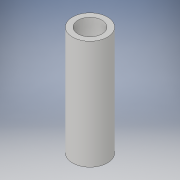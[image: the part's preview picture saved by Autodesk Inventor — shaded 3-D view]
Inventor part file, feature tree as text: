
AUTODESK INVENTOR PART (.ipt)
format: ipt  version: 2018 (Build 220112000, 112)  size: 97,280 bytes
history: native  units: in
note: dims shown in document units (in); Inventor stores cm internally (conversion verified against a paired STEP export)
features: sketch x2, extrude x1, hole x1
ambient origin geometry x8: Origin, YZ Plane, XZ Plane, XY Plane, X Axis, Y Axis, Z Axis, Center Point
bodies: Solid1 (feature_tree)
feature tree (4):
  extrude  "Extrusion1"  Depth=0.5in TaperAngle=0.0deg
  hole  "Hole1"  [1 undecoded]
  sketch  "Sketch1"  dims[d0=0.16in d1=0.5in d2=0.0in]
  sketch  "Sketch2"  dims[d3=0.11in d4=0.11in d5=0.75in d6=0.375in d7=0.25in d8=0.5635in d9=1.0in d10=0.8108in]
note: 1 required parameter value undecoded (feature->parameter linkage not recoverable at this tier; creation-order binding heuristic only, values carry confidence <= 0.55)
